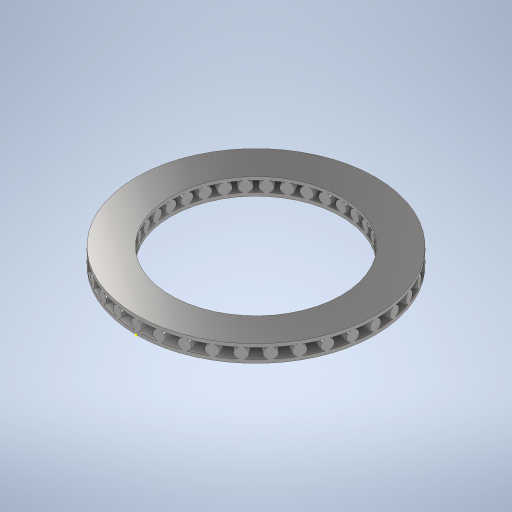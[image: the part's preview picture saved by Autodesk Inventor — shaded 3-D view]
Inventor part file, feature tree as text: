
AUTODESK INVENTOR PART (.ipt)
format: ipt  version: 2024.1 (Build 281209000, 209)  size: 646,656 bytes
history: native  units: in
note: dims shown in document units (in); Inventor stores cm internally (conversion verified against a paired STEP export)
features: sketch x5, extrude x4, plane x3, pattern_circular x1
ambient origin geometry x8: Origin, YZ Plane, XZ Plane, XY Plane, X Axis, Y Axis, Z Axis, Center Point
bodies: Solid1 (feature_tree)
feature tree (13):
  extrude  "Extrusion1"  Depth=1.9685in
  plane  "Work Plane1"
  extrude  "Extrusion2"  Depth=0.126in
  pattern_circular  "Circular Pattern1"  Count=36 Angle=360.0deg
  sketch  "Sketch3"  dims[d5=0.0984in]
  plane  "Work Plane3"
  extrude  "Extrusion3"  Depth=0.0394in TaperAngle=0.0deg
  extrude  "Extrusion4"  Depth=0.1969in
  sketch  "Sketch1"  dims[d0=2.7559in d1=1.9685in]
  sketch  "Sketch2"  dims[d2=0.0394in d3=0.0in d4=0.126in]
  plane  "Work Plane2"
  sketch  "Sketch4"  dims[d6=0.4562in d7=0.0in d8=14.1732in d9=360.0deg]
  sketch  "Sketch5"  dims[d11=-0.0039in d12=0.0394in d13=0.0in d14=0.1969in d15=0.0in d16=0.0in]
